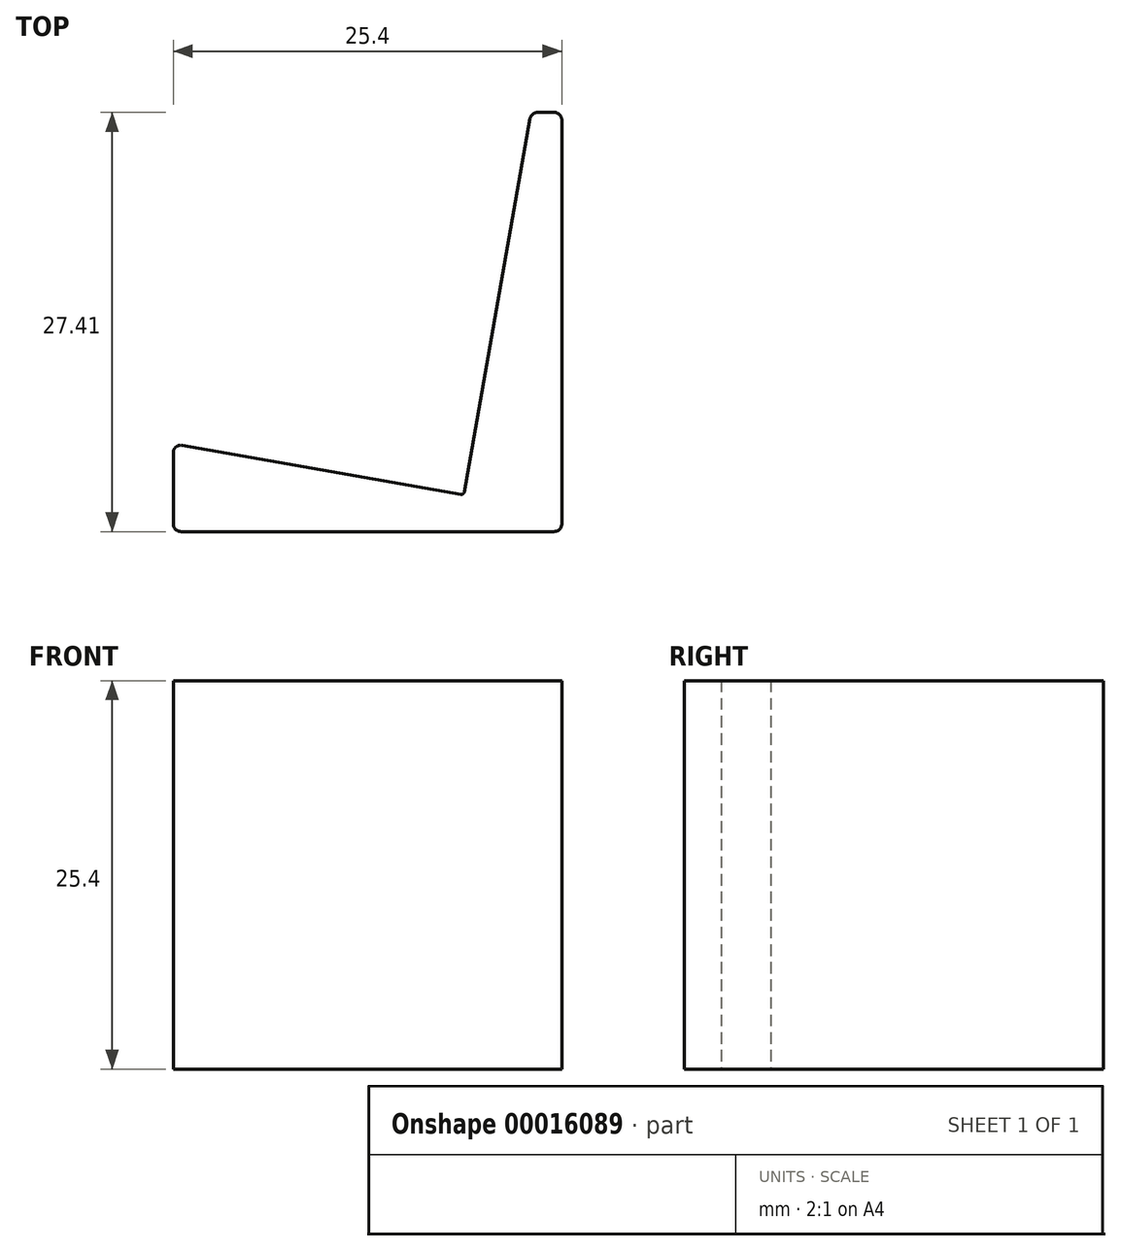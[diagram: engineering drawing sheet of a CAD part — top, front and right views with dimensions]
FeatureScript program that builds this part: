
annotation { "Feature Type Name" : "Feature", "Feature Type Description" : "" }
export const myFeature = defineFeature(function(context is Context, id is Id, definition is map)
    precondition{}
    {
        {
            var Q0;
            Q0=qCreatedBy(makeId("Top.planeOp"),FACE);
            var sketch = newSketch(context, id + "F0", { "sketchPlane" : qUnion([Q0])});
            skLineSegment(sketch, "E0", {"start": v(6.1, 2.43) * mm, "end": v(-12.11, 5.64) * mm});
            skLineSegment(sketch, "E1", {"start": v(-12.7, 5.15) * mm, "end": v(-12.7, 0) * mm});
            skLineSegment(sketch, "E2", {"start": v(-12.7, 0) * mm, "end": v(12.7, 0) * mm});
            skLineSegment(sketch, "E3", {"start": v(12.7, 0) * mm, "end": v(12.7, 26.91) * mm});
            skLineSegment(sketch, "E4", {"start": v(6.32, 2.6) * mm, "end": v(10.63, 27) * mm});
            skLineSegment(sketch, "E5", {"start": v(11.12, 27.41) * mm, "end": v(12.2, 27.41) * mm});
            skPoint(sketch, "E6.visualSharp", {"position": v(10.7, 27.41) * mm});
            skArc(sketch, "E6.filletArc", {"start": v(11.12, 27.41) * mm, "mid": v(10.8, 27.3) * mm, "end": v(10.63, 27) * mm});
            skPoint(sketch, "E7.visualSharp", {"position": v(12.7, 27.41) * mm});
            skArc(sketch, "E7.filletArc", {"start": v(12.7, 26.91) * mm, "mid": v(12.55, 27.27) * mm, "end": v(12.2, 27.41) * mm});
            skPoint(sketch, "E8.visualSharp", {"position": v(-12.7, 5.75) * mm});
            skArc(sketch, "E8.filletArc", {"start": v(-12.11, 5.64) * mm, "mid": v(-12.52, 5.54) * mm, "end": v(-12.7, 5.15) * mm});
            skPoint(sketch, "E9.visualSharp", {"position": v(6.29, 2.4) * mm});
            skArc(sketch, "E9.filletArc", {"start": v(6.1, 2.43) * mm, "mid": v(6.24, 2.47) * mm, "end": v(6.32, 2.6) * mm});
            skSolve(sketch);
        }
        {
            var Q0;
            Q0=qSketchRegion(id+"F0",true);
            var Q1;
            Q1=makeQuery(id+"F0.imprint","IMPRINT",FACE,{"disambiguationData":[TD([[makeQuery(id+"F0.imprint","IMPRINT",EDGE,{"derivedFrom":sQuery(id+"F0.wireOp",EDGE,"0de830e7-9daf-4a68-be67-74efd37edb9d.0")}),-1.0]])]});
            extrude(context, id + "F1", {"entities" : qUnion([Q0, Q1]), "depth" : 25.4 * mm});
        }
        {
            var Q0;
            Q0=makeQuery(id+"F1.opExtrude","SWEPT_EDGE",EDGE,{"disambiguationData":[OSD([sQuery(id+"F0.wireOp",EDGE,"E4"),sQuery(id+"F0.wireOp",EDGE,"E5")])]});
            var Q1;
            Q1=makeQuery(id+"F1.opExtrude","SWEPT_EDGE",EDGE,{"disambiguationData":[OSD([sQuery(id+"F0.wireOp",EDGE,"E0"),sQuery(id+"F0.wireOp",EDGE,"E1")])]});
            var Q2;
            Q2=makeQuery(id+"F1.opExtrude","SWEPT_EDGE",EDGE,{"disambiguationData":[OSD([sQuery(id+"F0.wireOp",EDGE,"E3"),sQuery(id+"F0.wireOp",EDGE,"E5")])]});
            fillet(context, id + "F2", {"entities" : qUnion([Q0, Q1, Q2]), "radius" : .5 * mm, "tangentPropagation" : true, "allowEdgeOverflow" : false});
        }
    });
